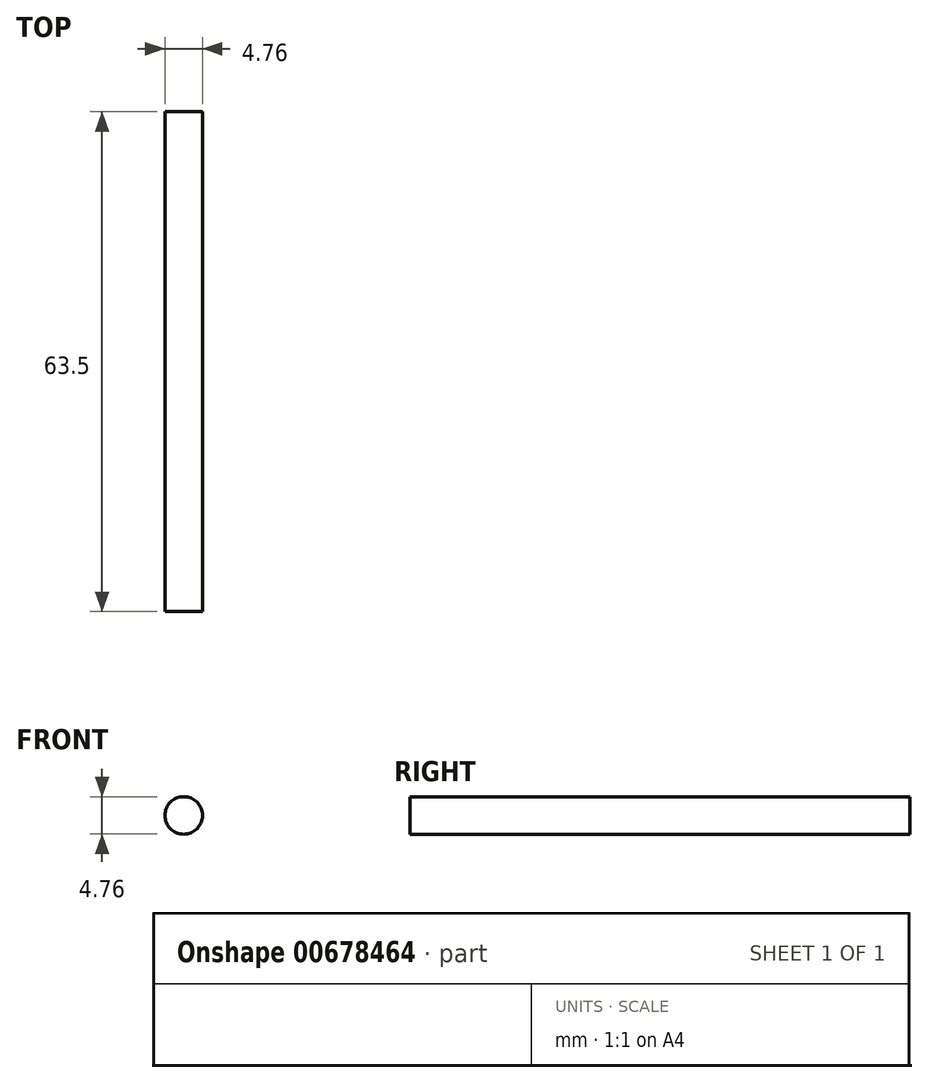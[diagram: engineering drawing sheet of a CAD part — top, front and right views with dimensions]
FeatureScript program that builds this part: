
annotation { "Feature Type Name" : "Feature", "Feature Type Description" : "" }
export const myFeature = defineFeature(function(context is Context, id is Id, definition is map)
    precondition{}
    {
        {
            var Q0;
            Q0=qCreatedBy(makeId("Front.planeOp"),FACE);
            var sketch = newSketch(context, id + "F0", { "sketchPlane" : qUnion([Q0])});
            skCircle(sketch, "E0", {"center": v(0, 0) * mm, "radius": 2.38 * mm});
            skSolve(sketch);
        }
        {
            var Q0;
            Q0=makeQuery(id+"F0.imprint","IMPRINT",FACE,{"disambiguationData":[TD([[makeQuery(id+"F0.imprint","IMPRINT",EDGE,{"derivedFrom":sQuery(id+"F0.wireOp",EDGE,"E0")}),1.0]])]});
            extrude(context, id + "F1", {"entities" : qUnion([Q0]), "oppositeDirection" : true, "depth" : 63.5 * mm, "offsetDistance" : 25.4 * mm});
        }
    });
